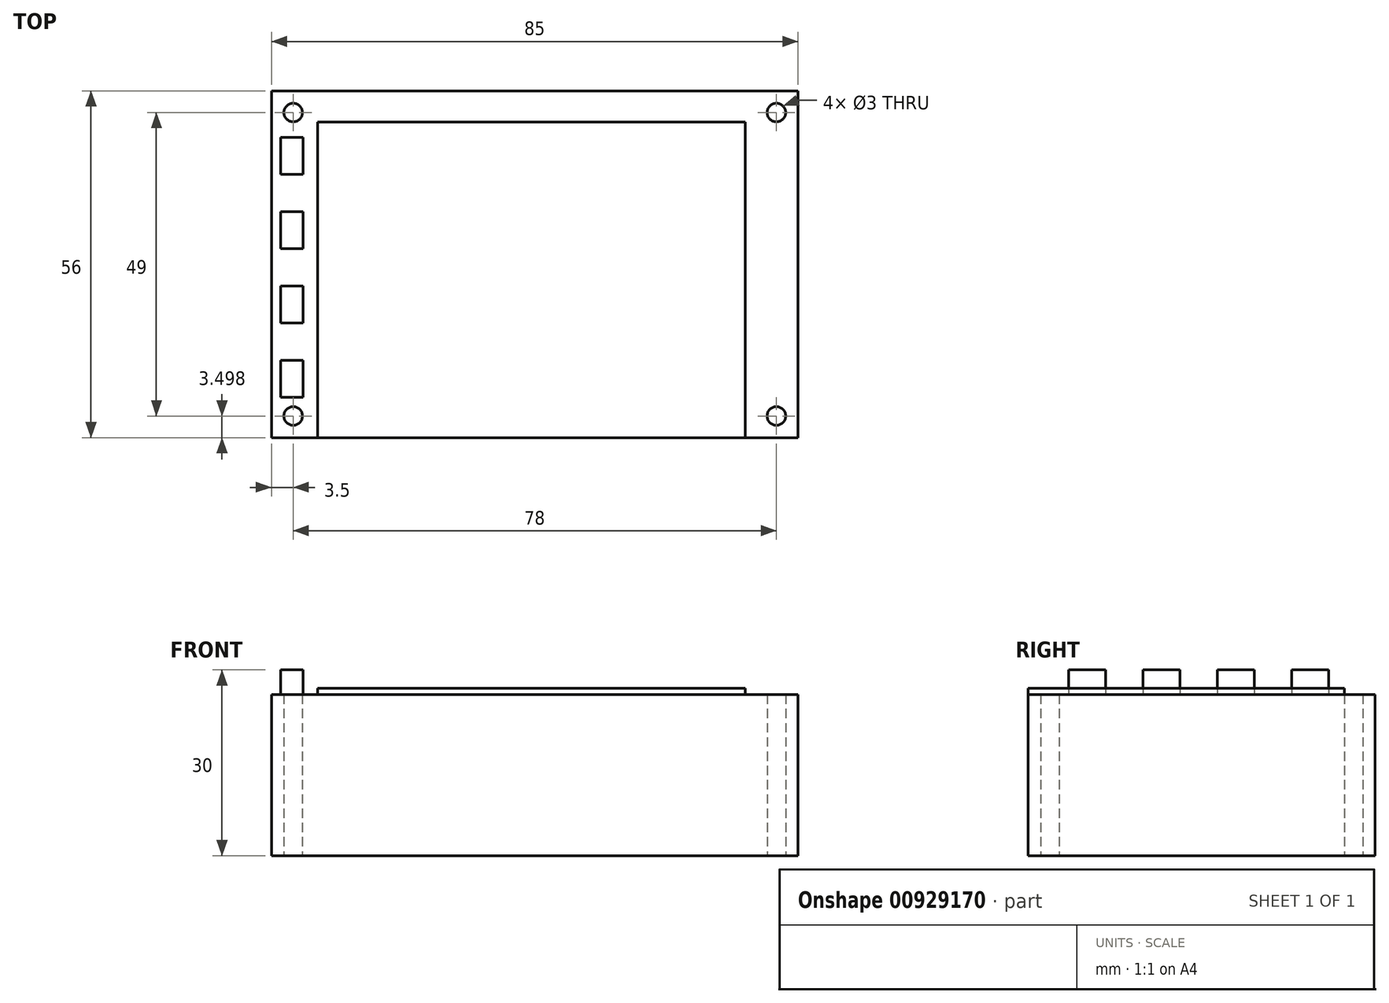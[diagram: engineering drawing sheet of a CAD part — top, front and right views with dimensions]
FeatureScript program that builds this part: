
annotation { "Feature Type Name" : "Feature", "Feature Type Description" : "" }
export const myFeature = defineFeature(function(context is Context, id is Id, definition is map)
    precondition{}
    {
        {
            var Q0;
            Q0=qCreatedBy(makeId("Top.planeOp"),FACE);
            var sketch = newSketch(context, id + "F0", { "sketchPlane" : qUnion([Q0])});
            skLineSegment(sketch, "E0.bottom", {"start": v(42.5, 24.49) * mm, "end": v(-42.5, 24.49) * mm});
            skLineSegment(sketch, "E0.top", {"start": v(42.5, -31.51) * mm, "end": v(-42.5, -31.51) * mm});
            skLineSegment(sketch, "E0.left", {"start": v(42.5, 24.49) * mm, "end": v(42.5, -31.51) * mm});
            skLineSegment(sketch, "E0.right", {"start": v(-42.5, 24.49) * mm, "end": v(-42.5, -31.51) * mm});
            skPoint(sketch, "E0.middle", {"position": v(0, -3.51) * mm});
            skCircle(sketch, "E1", {"center": v(-39, -28.01) * mm, "radius": 1.5 * mm});
            skCircle(sketch, "E2", {"center": v(-39, 20.99) * mm, "radius": 1.5 * mm});
            skCircle(sketch, "E3", {"center": v(39, 20.99) * mm, "radius": 1.5 * mm});
            skCircle(sketch, "E4", {"center": v(39, -28.01) * mm, "radius": 1.5 * mm});
            skSolve(sketch);
        }
        {
            var Q0;
            Q0=makeQuery(id+"F0.imprint","IMPRINT",FACE,{"disambiguationData":[TD([[makeQuery(id+"F0.imprint","IMPRINT",EDGE,{"derivedFrom":sQuery(id+"F0.wireOp",EDGE,"E0.bottom")}),1.0]])]});
            extrude(context, id + "F1", {"entities" : qUnion([Q0]), "depth" : 26 * mm, "offsetDistance" : 25 * mm});
        }
        {
            var Q0;
            Q0=makeQuery(id+"F1.opExtrude","CAP_FACE",FACE,{"disambiguationData":[OSD([sQuery(id+"F0.wireOp",EDGE,"E0.bottom"),sQuery(id+"F0.wireOp",EDGE,"E0.top"),sQuery(id+"F0.wireOp",EDGE,"E0.left"),sQuery(id+"F0.wireOp",EDGE,"E0.right")])],"isStart":false});
            var sketch = newSketch(context, id + "F2", { "sketchPlane" : qUnion([Q0])});
            skLineSegment(sketch, "E5.bottom", {"start": v(-35.04, -31.51) * mm, "end": v(33.96, -31.51) * mm});
            skLineSegment(sketch, "E5.top", {"start": v(-35.04, 19.49) * mm, "end": v(33.96, 19.49) * mm});
            skLineSegment(sketch, "E5.left", {"start": v(-35.04, -31.51) * mm, "end": v(-35.04, 19.49) * mm});
            skLineSegment(sketch, "E5.right", {"start": v(33.96, -31.51) * mm, "end": v(33.96, 19.49) * mm});
            skPoint(sketch, "E5.middle", {"position": v(-0.54, -6.01) * mm});
            skSolve(sketch);
        }
        {
            var Q0;
            Q0=makeQuery(id+"F2.imprint","IMPRINT",FACE,{"disambiguationData":[TD([[makeQuery(id+"F2.imprint","IMPRINT",EDGE,{"derivedFrom":sQuery(id+"F2.wireOp",EDGE,"E5.bottom")}),-1.0]])]});
            extrude(context, id + "F3", {"entities" : qUnion([Q0]), "depth" : 1 * mm, "offsetDistance" : 25 * mm});
        }
        {
            var Q0;
            Q0=makeQuery(id+"F1.opExtrude","CAP_FACE",FACE,{"disambiguationData":[OSD([sQuery(id+"F0.wireOp",EDGE,"E0.bottom"),sQuery(id+"F0.wireOp",EDGE,"E0.top"),sQuery(id+"F0.wireOp",EDGE,"E0.left"),sQuery(id+"F0.wireOp",EDGE,"E0.right"),sQuery(id+"F0.wireOp",EDGE,"E1"),sQuery(id+"F0.wireOp",EDGE,"E2"),sQuery(id+"F0.wireOp",EDGE,"E3"),sQuery(id+"F0.wireOp",EDGE,"E4")])],"isStart":false});
            var sketch = newSketch(context, id + "F4", { "sketchPlane" : qUnion([Q0])});
            skLineSegment(sketch, "E6.bottom", {"start": v(-41, 16.99) * mm, "end": v(-37.4, 16.99) * mm});
            skLineSegment(sketch, "E6.top", {"start": v(-41, 10.99) * mm, "end": v(-37.4, 10.99) * mm});
            skLineSegment(sketch, "E6.left", {"start": v(-41, 16.99) * mm, "end": v(-41, 10.99) * mm});
            skLineSegment(sketch, "E6.right", {"start": v(-37.4, 16.99) * mm, "end": v(-37.4, 10.99) * mm});
            skLineSegment(sketch, "E7.bottom", {"start": v(-41, -1.01) * mm, "end": v(-37.4, -1.01) * mm});
            skLineSegment(sketch, "E7.top", {"start": v(-41, 4.99) * mm, "end": v(-37.4, 4.99) * mm});
            skLineSegment(sketch, "E7.left", {"start": v(-41, -1.01) * mm, "end": v(-41, 4.99) * mm});
            skLineSegment(sketch, "E7.right", {"start": v(-37.4, -1.01) * mm, "end": v(-37.4, 4.99) * mm});
            skLineSegment(sketch, "E8.bottom", {"start": v(-41, -13.01) * mm, "end": v(-37.4, -13.01) * mm});
            skLineSegment(sketch, "E8.top", {"start": v(-41, -7.01) * mm, "end": v(-37.4, -7.01) * mm});
            skLineSegment(sketch, "E8.left", {"start": v(-41, -13.01) * mm, "end": v(-41, -7.01) * mm});
            skLineSegment(sketch, "E8.right", {"start": v(-37.4, -13.01) * mm, "end": v(-37.4, -7.01) * mm});
            skLineSegment(sketch, "E9.bottom", {"start": v(-41, -25.01) * mm, "end": v(-37.4, -25.01) * mm});
            skLineSegment(sketch, "E9.top", {"start": v(-41, -19.01) * mm, "end": v(-37.4, -19.01) * mm});
            skLineSegment(sketch, "E9.left", {"start": v(-41, -25.01) * mm, "end": v(-41, -19.01) * mm});
            skLineSegment(sketch, "E9.right", {"start": v(-37.4, -25.01) * mm, "end": v(-37.4, -19.01) * mm});
            skSolve(sketch);
        }
        {
            var Q0;
            Q0 = qSketchRegion(id + "F4", true);
            extrude(context, id + "F5", {"entities" : qUnion([Q0]), "operationType" : NewBodyOperationType.ADD, "depth" : 4 * mm, "offsetDistance" : 25 * mm});
        }
    });
